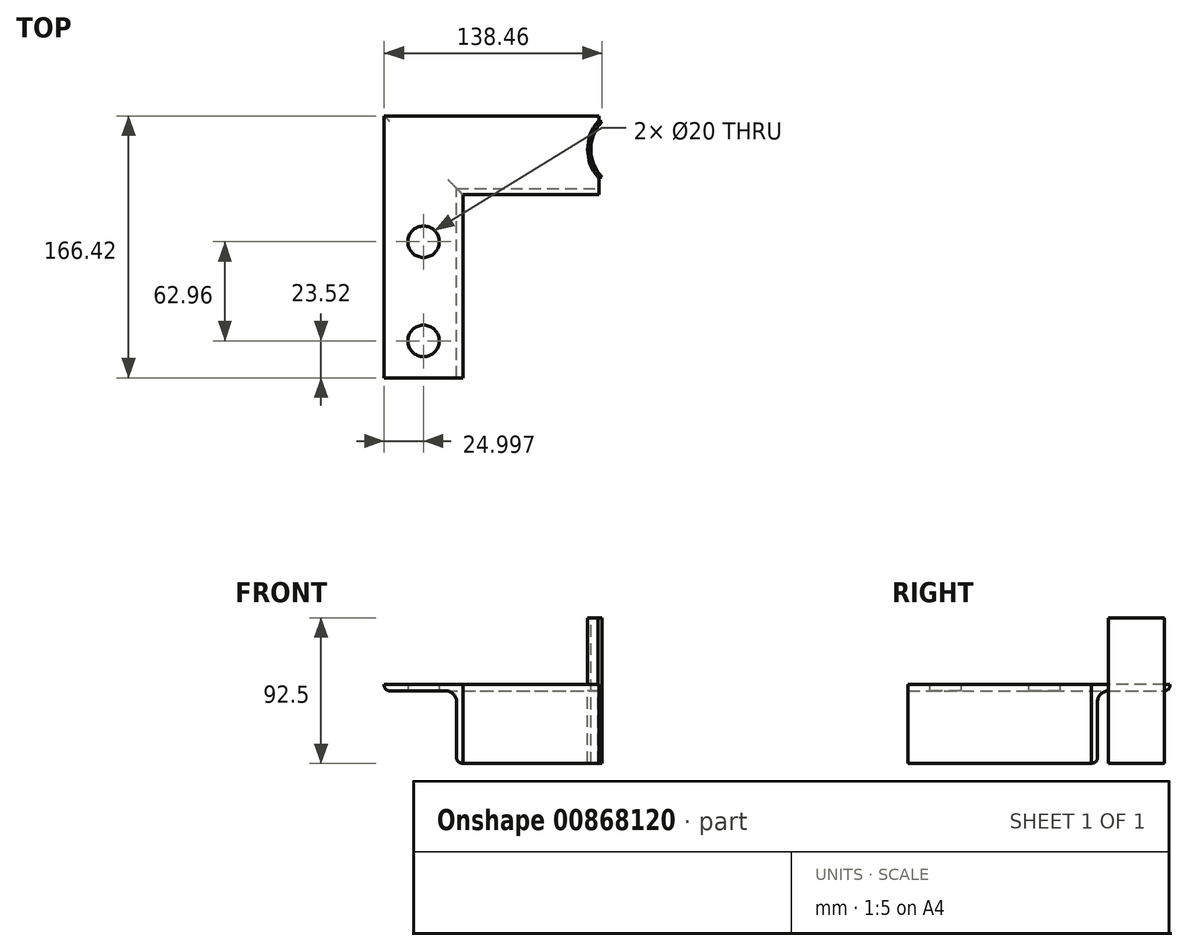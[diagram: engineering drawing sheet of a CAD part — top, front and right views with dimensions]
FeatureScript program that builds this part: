
annotation { "Feature Type Name" : "Feature", "Feature Type Description" : "" }
export const myFeature = defineFeature(function(context is Context, id is Id, definition is map)
    precondition{}
    {
        {
            var Q0;
            Q0=qCreatedBy(makeId("Front.planeOp"),FACE);
            var sketch = newSketch(context, id + "F0", { "sketchPlane" : qUnion([Q0])});
            skLineSegment(sketch, "E0", {"start": v(-36.42, 13.58) * mm, "end": v(13.58, 13.58) * mm});
            skLineSegment(sketch, "E1", {"start": v(13.58, 13.58) * mm, "end": v(13.58, -36.42) * mm});
            skLineSegment(sketch, "E2", {"start": v(9.58, -36.42) * mm, "end": v(9.58, 9.58) * mm});
            skLineSegment(sketch, "E3", {"start": v(9.58, 9.58) * mm, "end": v(-36.42, 9.58) * mm});
            skLineSegment(sketch, "E4", {"start": v(0, 48.56) * mm, "end": v(0, -41.19) * mm, "construction": true});
            skLineSegment(sketch, "E5", {"start": v(-40.22, 0) * mm, "end": v(47.92, 0) * mm, "construction": true});
            skLineSegment(sketch, "E6", {"start": v(0, 0) * mm, "end": v(34.3, 34.3) * mm, "construction": true});
            skLineSegment(sketch, "E7", {"start": v(-36.42, 9.58) * mm, "end": v(-36.42, 13.58) * mm});
            skLineSegment(sketch, "E8", {"start": v(9.58, -36.42) * mm, "end": v(13.58, -36.42) * mm});
            skSolve(sketch);
        }
        {
            var Q0;
            Q0=qCreatedBy(makeId("Top.planeOp"),FACE);
            var sketch = newSketch(context, id + "F1", { "sketchPlane" : qUnion([Q0])});
            skLineSegment(sketch, "E9", {"start": v(0, 0) * mm, "end": v(0, 130) * mm});
            skLineSegment(sketch, "E10", {"start": v(0, 130) * mm, "end": v(100, 130) * mm});
            skSolve(sketch);
        }
        {
            var Q0;
            Q0=makeQuery(id+"F0.imprint","IMPRINT",FACE,{"disambiguationData":[TD([[makeQuery(id+"F0.imprint","IMPRINT",EDGE,{"derivedFrom":sQuery(id+"F0.wireOp",EDGE,"E0")}),-1.0]])]});
            var Q1;
            Q1=sQuery(id+"F1.wireOp",EDGE,"E9");
            var Q2;
            Q2=sQuery(id+"F1.wireOp",EDGE,"E10");
            sweep(context, id + "F2", {"profiles" : qUnion([Q0]), "path" : qUnion([Q1, Q2])});
        }
        {
            var Q0;
            Q0=makeQuery(id+"F2.opSweep","SWEPT_EDGE",EDGE,{"disambiguationData":[OSD([sQuery(id+"F0.wireOp",EDGE,"E2"),sQuery(id+"F0.wireOp",EDGE,"E8"),sQuery(id+"F1.wireOp",EDGE,"wX8RXHP5-JrQV-AEwV-USVR-1wF8GxR78Qcj")])]});
            var Q1;
            Q1=makeQuery(id+"F2.opSweep","SWEPT_EDGE",EDGE,{"disambiguationData":[OSD([sQuery(id+"F0.wireOp",EDGE,"E3"),sQuery(id+"F0.wireOp",EDGE,"E7"),sQuery(id+"F1.wireOp",EDGE,"wX8RXHP5-JrQV-AEwV-USVR-1wF8GxR78Qcj")])]});
            var Q2;
            Q2=makeQuery(id+"F2.opSweep","SWEPT_EDGE",EDGE,{"disambiguationData":[OSD([sQuery(id+"F0.wireOp",EDGE,"E2"),sQuery(id+"F0.wireOp",EDGE,"E8"),sQuery(id+"F1.wireOp",EDGE,"8aWFVj7g-Txpx-71sT-GaHg-KEv052FT9ujs")])]});
            var Q3;
            Q3=makeQuery(id+"F2.opSweep","SWEPT_EDGE",EDGE,{"disambiguationData":[OSD([sQuery(id+"F0.wireOp",EDGE,"E3"),sQuery(id+"F0.wireOp",EDGE,"E7"),sQuery(id+"F1.wireOp",EDGE,"8aWFVj7g-Txpx-71sT-GaHg-KEv052FT9ujs")])]});
            fillet(context, id + "F3", {"entities" : qUnion([Q0, Q1, Q2, Q3]), "radius" : 3.5 * mm, "tangentPropagation" : true, "allowEdgeOverflow" : false});
        }
        {
            var Q0;
            Q0=makeQuery(id+"F2.opSweep","SWEPT_EDGE",EDGE,{"disambiguationData":[OSD([sQuery(id+"F0.wireOp",EDGE,"E2"),sQuery(id+"F0.wireOp",EDGE,"E3"),sQuery(id+"F1.wireOp",EDGE,"wX8RXHP5-JrQV-AEwV-USVR-1wF8GxR78Qcj")])]});
            var Q1;
            Q1=makeQuery(id+"F2.opSweep","SWEPT_EDGE",EDGE,{"disambiguationData":[OSD([sQuery(id+"F0.wireOp",EDGE,"E2"),sQuery(id+"F0.wireOp",EDGE,"E3"),sQuery(id+"F1.wireOp",EDGE,"8aWFVj7g-Txpx-71sT-GaHg-KEv052FT9ujs")])]});
            fillet(context, id + "F4", {"entities" : qUnion([Q0, Q1]), "radius" : 7 * mm, "tangentPropagation" : true, "allowEdgeOverflow" : false});
        }
        {
            var Q0;
            Q0=makeQuery(id+"F2.opSweep","SWEPT_FACE",FACE,{"disambiguationData":[OSD([sQuery(id+"F0.wireOp",EDGE,"E3"),sQuery(id+"F1.wireOp",EDGE,"E9")])]});
            var sketch = newSketch(context, id + "F5", { "sketchPlane" : qUnion([Q0])});
            skLineSegment(sketch, "E11", {"start": v(100, -163.67) * mm, "end": v(100, -126.67) * mm});
            skArc(sketch, "E12", {"start": v(100, -126.67) * mm, "mid": v(92.85, -145.17) * mm, "end": v(100, -163.67) * mm});
            skSolve(sketch);
        }
        {
            var Q0;
            {var subQ0=sQuery(id+"F5.wireOp",EDGE,"E11");var subQ1=sQuery(id+"F0.wireOp",EDGE,"E3");var subQ2=makeQuery(id+"F2.opSweep","SWEPT_FACE",FACE,{"disambiguationData":[OSD([subQ1,sQuery(id+"F1.wireOp",EDGE,"E9")])]});var subQ3=sQuery(id+"F1.wireOp",EDGE,"E10");var subQ4=makeQuery(id+"F3.opFillet","BLEND_EDGE",EDGE,{"blendedFrom":[makeQuery(id+"F2.opSweep","SWEPT_EDGE",EDGE,{"disambiguationData":[OSD([subQ1,sQuery(id+"F0.wireOp",EDGE,"E7"),subQ3])]}),subQ2],"blendedInto":[subQ2]});var subQ5=makeQuery(id+"F5.imprint","INTERSECT",VERTEX,{"derivedFrom":[subQ4,subQ0]});var subQ6=makeQuery(id+"F4.opFillet","BLEND_EDGE",EDGE,{"blendedFrom":[makeQuery(id+"F2.opSweep","SWEPT_EDGE",EDGE,{"disambiguationData":[OSD([sQuery(id+"F0.wireOp",EDGE,"E2"),subQ1,subQ3])]}),subQ2],"blendedInto":[subQ2]});var subQ7=makeQuery(id+"F5.imprint","INTERSECT",VERTEX,{"derivedFrom":[subQ6,subQ0]});Q0=makeQuery(id+"F5.imprint","IMPRINT",FACE,{"disambiguationData":[TD([[makeQuery(id+"F5.imprint","IMPRINT",EDGE,{"disambiguationData":[TD([[subQ5,1.0],[subQ7,-1.0]])],"derivedFrom":subQ0}),-1.0]])]});}
            extrude(context, id + "F6", {"entities" : qUnion([Q0]), "operationType" : NewBodyOperationType.REMOVE, "oppositeDirection" : true, "depth" : 25 * mm, "offsetDistance" : 25 * mm});
        }
        {
            var Q0;
            Q0=makeQuery(id+"F2.opSweep","SWEPT_FACE",FACE,{"disambiguationData":[OSD([sQuery(id+"F0.wireOp",EDGE,"E3"),sQuery(id+"F1.wireOp",EDGE,"E9")])]});
            var sketch = newSketch(context, id + "F7", { "sketchPlane" : qUnion([Q0])});
            skLineSegment(sketch, "E13", {"start": v(102.04, -127.42) * mm, "end": v(102.04, -162.92) * mm});
            skLineSegment(sketch, "E14", {"start": v(99.34, -127.42) * mm, "end": v(102.04, -127.42) * mm});
            skLineSegment(sketch, "E15", {"start": v(99.34, -162.92) * mm, "end": v(102.04, -162.92) * mm});
            skArc(sketch, "E16", {"start": v(102.04, -127.42) * mm, "mid": v(94.85, -145.17) * mm, "end": v(102.04, -162.92) * mm});
            skSolve(sketch);
        }
        {
            var Q0;
            {var subQ7=sQuery(id+"F7.wireOp",EDGE,"E14");Q0=makeQuery(id+"F7.imprint","IMPRINT",FACE,{"disambiguationData":[TD([[makeQuery(id+"F7.imprint","IMPRINT",EDGE,{"derivedFrom":subQ7}),-1.0]])]});}
            extrude(context, id + "F8", {"entities" : qUnion([Q0]), "operationType" : NewBodyOperationType.ADD, "endBound" : BoundingType.SYMMETRIC, "depth" : 92.5 * mm, "offsetDistance" : 25 * mm});
        }
        {
            var Q0;
            Q0=makeQuery(id+"F2.opSweep","SWEPT_FACE",FACE,{"disambiguationData":[OSD([sQuery(id+"F0.wireOp",EDGE,"E3"),sQuery(id+"F1.wireOp",EDGE,"E9")])]});
            var sketch = newSketch(context, id + "F9", { "sketchPlane" : qUnion([Q0])});
            skLineSegment(sketch, "E17.bottom", {"start": v(-32.42, 0) * mm, "end": v(2.58, 0) * mm, "construction": true});
            skLineSegment(sketch, "E17.top", {"start": v(-32.42, -110) * mm, "end": v(2.58, -110) * mm, "construction": true});
            skLineSegment(sketch, "E17.left", {"start": v(-32.42, 0) * mm, "end": v(-32.42, -110) * mm, "construction": true});
            skLineSegment(sketch, "E17.right", {"start": v(2.58, 0) * mm, "end": v(2.58, -110) * mm, "construction": true});
            skLineSegment(sketch, "E18", {"start": v(-32.42, -55) * mm, "end": v(2.58, -55) * mm, "construction": true});
            skLineSegment(sketch, "E19", {"start": v(-14.92, 0) * mm, "end": v(-14.92, -55) * mm, "construction": true});
            skLineSegment(sketch, "E20", {"start": v(-14.92, -55) * mm, "end": v(-14.92, -110) * mm, "construction": true});
            skCircle(sketch, "E21", {"center": v(-11.42, -23.52) * mm, "radius": 10 * mm});
            skCircle(sketch, "E22", {"center": v(-11.42, -86.48) * mm, "radius": 10 * mm});
            skLineSegment(sketch, "E23", {"start": v(-11.42, -23.52) * mm, "end": v(-11.42, -86.48) * mm, "construction": true});
            skLineSegment(sketch, "E24", {"start": v(-14.92, -86.48) * mm, "end": v(-1.42, -86.48) * mm, "construction": true});
            skLineSegment(sketch, "E25", {"start": v(-14.92, -23.52) * mm, "end": v(-1.42, -23.52) * mm, "construction": true});
            skSolve(sketch);
        }
        {
            var Q0;
            Q0=makeQuery(id+"F9.imprint","IMPRINT",FACE,{"disambiguationData":[TD([[makeQuery(id+"F9.imprint","IMPRINT",EDGE,{"derivedFrom":sQuery(id+"F9.wireOp",EDGE,"E21")}),1.0]])]});
            var Q1;
            Q1=makeQuery(id+"F9.imprint","IMPRINT",FACE,{"disambiguationData":[TD([[makeQuery(id+"F9.imprint","IMPRINT",EDGE,{"derivedFrom":sQuery(id+"F9.wireOp",EDGE,"E22")}),1.0]])]});
            extrude(context, id + "F10", {"entities" : qUnion([Q0, Q1]), "operationType" : NewBodyOperationType.REMOVE, "oppositeDirection" : true, "depth" : 25 * mm, "offsetDistance" : 25 * mm});
        }
    });
